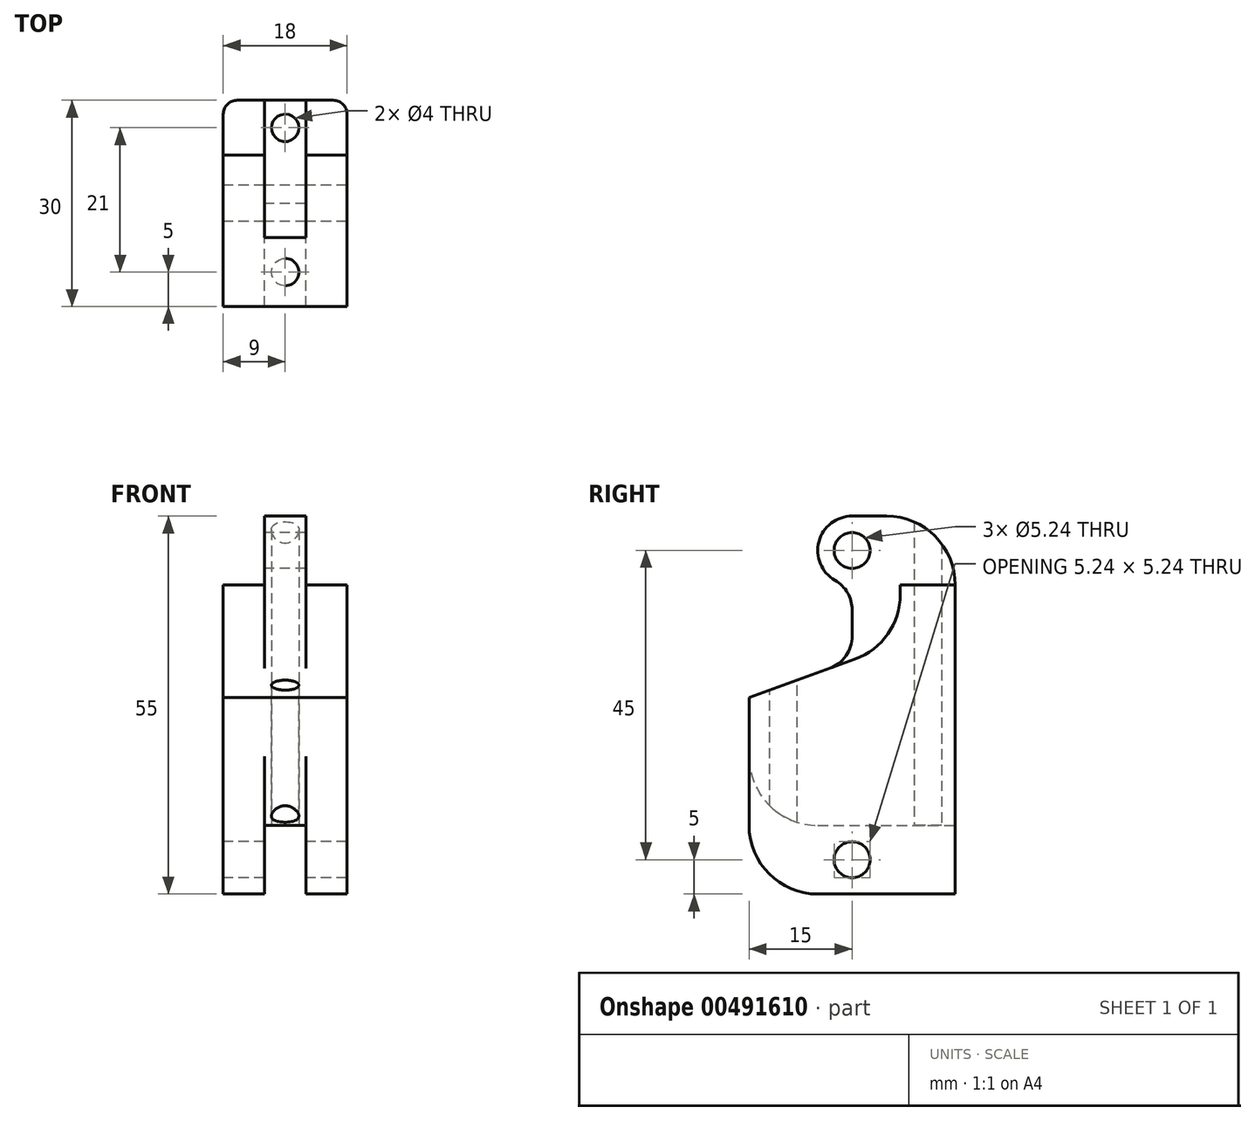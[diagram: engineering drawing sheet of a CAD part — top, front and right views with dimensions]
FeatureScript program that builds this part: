
annotation { "Feature Type Name" : "Feature", "Feature Type Description" : "" }
export const myFeature = defineFeature(function(context is Context, id is Id, definition is map)
    precondition{}
    {
        {
            var Q0;
            Q0=qCreatedBy(makeId("Front.planeOp"),FACE);
            var sketch = newSketch(context, id + "F0", { "sketchPlane" : qUnion([Q0])});
            skLineSegment(sketch, "E0.bottom", {"start": v(9, 17.5) * mm, "end": v(3, 17.5) * mm});
            skLineSegment(sketch, "E0.top", {"start": v(3, -17.5) * mm, "end": v(-3, -17.5) * mm});
            skLineSegment(sketch, "E0.left", {"start": v(9, 17.5) * mm, "end": v(9, -17.5) * mm});
            skLineSegment(sketch, "E0.right", {"start": v(-9, 17.5) * mm, "end": v(-9, -17.5) * mm});
            skPoint(sketch, "E0.middle", {"position": v(0, 0) * mm});
            skLineSegment(sketch, "E1.bottom", {"start": v(3, 27.5) * mm, "end": v(-3, 27.5) * mm});
            skLineSegment(sketch, "E1.left", {"start": v(3, 27.5) * mm, "end": v(3, 17.5) * mm});
            skLineSegment(sketch, "E1.right", {"start": v(-3, 27.5) * mm, "end": v(-3, 17.5) * mm});
            skPoint(sketch, "E1.middle", {"position": v(0, 17.5) * mm});
            skLineSegment(sketch, "E2.top", {"start": v(-9, -27.5) * mm, "end": v(-3, -27.5) * mm});
            skLineSegment(sketch, "E2.right", {"start": v(-3, -17.5) * mm, "end": v(-3, -27.5) * mm});
            skLineSegment(sketch, "E3.MirrorCS", {"start": v(3, -17.5) * mm, "end": v(3, -27.5) * mm});
            skLineSegment(sketch, "E4.MirrorCS", {"start": v(9, -27.5) * mm, "end": v(3, -27.5) * mm});
            skLineSegment(sketch, "E5.MirrorCS", {"start": v(9, -17.5) * mm, "end": v(9, -27.5) * mm});
            skLineSegment(sketch, "E6.trimOffspring", {"start": v(-3, 17.5) * mm, "end": v(-9, 17.5) * mm});
            skLineSegment(sketch, "E7", {"start": v(-9, -17.5) * mm, "end": v(-9, -27.5) * mm});
            skSolve(sketch);
        }
        {
            var Q0;
            Q0=makeQuery(id+"F0.imprint","IMPRINT",FACE,{"disambiguationData":[TD([[makeQuery(id+"F0.imprint","IMPRINT",EDGE,{"derivedFrom":sQuery(id+"F0.wireOp",EDGE,"E0.bottom")}),1.0]])]});
            extrude(context, id + "F1", {"entities" : qUnion([Q0]), "depth" : 30 * mm, "symmetric" : true});
        }
        {
            var Q0;
            Q0=makeQuery(id+"F1.opExtrude","SWEPT_FACE",FACE,{"disambiguationData":[OSD([sQuery(id+"F0.wireOp",EDGE,"E1.right")])]});
            var sketch = newSketch(context, id + "F2", { "sketchPlane" : qUnion([Q0])});
            skLineSegment(sketch, "E8", {"start": v(0, 17.5) * mm, "end": v(0, 27.5) * mm});
            skCircle(sketch, "E9", {"center": v(0, 22.5) * mm, "radius": 2.62 * mm});
            skSolve(sketch);
        }
        {
            var Q0;
            Q0=qSketchRegion(id+"F2",true);
            extrude(context, id + "F3", {"entities" : qUnion([Q0]), "operationType" : NewBodyOperationType.REMOVE, "oppositeDirection" : true, "depth" : 6 * mm});
        }
        {
            var Q0;
            Q0=makeQuery(id+"F1.opExtrude","SWEPT_FACE",FACE,{"disambiguationData":[OSD([sQuery(id+"F0.wireOp",EDGE,"E0.right"),sQuery(id+"F0.wireOp",EDGE,"E7")])]});
            var sketch = newSketch(context, id + "F4", { "sketchPlane" : qUnion([Q0])});
            skPoint(sketch, "E10.endSnap0", {"position": v(0, -27.5) * mm});
            skCircle(sketch, "E11", {"center": v(0, -22.5) * mm, "radius": 2.62 * mm});
            skLineSegment(sketch, "E12", {"start": v(0, -27.5) * mm, "end": v(0, -22.5) * mm});
            skSolve(sketch);
        }
        {
            var Q0;
            Q0=qSketchRegion(id+"F4",true);
            extrude(context, id + "F5", {"entities" : qUnion([Q0]), "operationType" : NewBodyOperationType.REMOVE, "oppositeDirection" : true, "depth" : 18 * mm});
        }
        {
            var Q0;
            Q0=makeQuery(id+"F1.opExtrude","CAP_EDGE",EDGE,{"disambiguationData":[OSD([sQuery(id+"F0.wireOp",EDGE,"E1.bottom")])],"isStart":true});
            var Q1;
            Q1=makeQuery(id+"F1.opExtrude","CAP_EDGE",EDGE,{"disambiguationData":[OSD([sQuery(id+"F0.wireOp",EDGE,"E1.bottom")])],"isStart":false});
            var Q2;
            Q2=makeQuery(id+"F1.opExtrude","CAP_EDGE",EDGE,{"disambiguationData":[OSD([sQuery(id+"F0.wireOp",EDGE,"E4.MirrorCS")])],"isStart":false});
            var Q3;
            Q3=makeQuery(id+"F1.opExtrude","CAP_EDGE",EDGE,{"disambiguationData":[OSD([sQuery(id+"F0.wireOp",EDGE,"E2.top")])],"isStart":false});
            fillet(context, id + "F6", {"entities" : qUnion([Q0, Q1, Q2, Q3]), "radius" : 10 * mm, "tangentPropagation" : true, "allowEdgeOverflow" : false});
        }
        {
            var Q0;
            Q0=makeQuery(id+"F1.opExtrude","SWEPT_FACE",FACE,{"disambiguationData":[OSD([sQuery(id+"F0.wireOp",EDGE,"E0.left"),sQuery(id+"F0.wireOp",EDGE,"E5.MirrorCS")])]});
            var sketch = newSketch(context, id + "F7", { "sketchPlane" : qUnion([Q0])});
            skPoint(sketch, "E13.endSnap0", {"position": v(0, 17.5) * mm});
            skLineSegment(sketch, "E14", {"start": v(-15, 17.5) * mm, "end": v(-15, 1.08) * mm});
            skLineSegment(sketch, "E15", {"start": v(-15, 17.5) * mm, "end": v(7, 17.5) * mm});
            skLineSegment(sketch, "E16", {"start": v(-15, 1.08) * mm, "end": v(15, 1.08) * mm});
            skLineSegment(sketch, "E17", {"start": v(-15, 1.08) * mm, "end": v(0.42, 6.7) * mm});
            skLineSegment(sketch, "E18", {"start": v(7, 17.5) * mm, "end": v(7, 16.09) * mm});
            skPoint(sketch, "E19.visualSharp", {"position": v(7, 9.09) * mm});
            skArc(sketch, "E19.filletArc", {"start": v(0.42, 6.7) * mm, "mid": v(5.2, 10.35) * mm, "end": v(7, 16.09) * mm});
            skSolve(sketch);
        }
        {
            var Q0;
            Q0=makeQuery(id+"F1.opExtrude","SWEPT_FACE",FACE,{"disambiguationData":[OSD([sQuery(id+"F0.wireOp",EDGE,"E0.right"),sQuery(id+"F0.wireOp",EDGE,"E7")])]});
            var sketch = newSketch(context, id + "F8", { "sketchPlane" : qUnion([Q0])});
            skLineSegment(sketch, "E20", {"start": v(-0.42, 6.7) * mm, "end": v(15, 1.08) * mm});
            skLineSegment(sketch, "E21", {"start": v(15, 1.08) * mm, "end": v(15, 17.5) * mm});
            skLineSegment(sketch, "E22", {"start": v(15, 1.08) * mm, "end": v(-15, 1.08) * mm});
            skLineSegment(sketch, "E23", {"start": v(15, 17.5) * mm, "end": v(-7, 17.5) * mm});
            skLineSegment(sketch, "E24", {"start": v(-7, 17.5) * mm, "end": v(-7, 16.09) * mm});
            skPoint(sketch, "E25.visualSharp", {"position": v(-7, 9.09) * mm});
            skArc(sketch, "E25.filletArc", {"start": v(-7, 16.09) * mm, "mid": v(-5.2, 10.35) * mm, "end": v(-0.42, 6.7) * mm});
            skSolve(sketch);
        }
        {
            var Q0;
            Q0=makeQuery(id+"F8.imprint","IMPRINT",FACE,{"disambiguationData":[TD([[makeQuery(id+"F8.imprint","IMPRINT",EDGE,{"derivedFrom":sQuery(id+"F8.wireOp",EDGE,"E20")}),1.0]])]});
            extrude(context, id + "F9", {"entities" : qUnion([Q0]), "operationType" : NewBodyOperationType.REMOVE, "oppositeDirection" : true, "depth" : 6 * mm});
        }
        {
            var Q0;
            Q0=makeQuery(id+"F7.imprint","IMPRINT",FACE,{"disambiguationData":[TD([[makeQuery(id+"F7.imprint","IMPRINT",EDGE,{"derivedFrom":sQuery(id+"F7.wireOp",EDGE,"E14")}),1.0]])]});
            extrude(context, id + "F10", {"entities" : qUnion([Q0]), "operationType" : NewBodyOperationType.REMOVE, "oppositeDirection" : true, "depth" : 6 * mm});
        }
        {
            var Q0;
            Q0=makeQuery(id+"F1.opExtrude","CAP_EDGE",EDGE,{"disambiguationData":[OSD([sQuery(id+"F0.wireOp",EDGE,"E0.left"),sQuery(id+"F0.wireOp",EDGE,"E5.MirrorCS")])],"isStart":true});
            var Q1;
            Q1=makeQuery(id+"F1.opExtrude","CAP_EDGE",EDGE,{"disambiguationData":[OSD([sQuery(id+"F0.wireOp",EDGE,"E0.right"),sQuery(id+"F0.wireOp",EDGE,"E7")])],"isStart":true});
            fillet(context, id + "F11", {"entities" : qUnion([Q0, Q1]), "radius" : 2 * mm, "tangentPropagation" : true, "allowEdgeOverflow" : false});
        }
        {
            var Q0;
            Q0=makeQuery(id+"F9.boolean.opBoolean","MERGE",FACE,{"derivedFrom":[makeQuery(id+"F1.opExtrude","SWEPT_FACE",FACE,{"disambiguationData":[OSD([sQuery(id+"F0.wireOp",EDGE,"E1.right")])]}),makeQuery(id+"F9.opExtrude","CAP_FACE",FACE,{"disambiguationData":[OSD([sQuery(id+"F8.wireOp",EDGE,"E20"),sQuery(id+"F8.wireOp",EDGE,"E21"),sQuery(id+"F8.wireOp",EDGE,"E23"),sQuery(id+"F8.wireOp",EDGE,"E24"),sQuery(id+"F8.wireOp",EDGE,"E25.filletArc")])],"isStart":false})]});
            var sketch = newSketch(context, id + "F12", { "sketchPlane" : qUnion([Q0])});
            skLineSegment(sketch, "E26", {"start": v(0, 27.5) * mm, "end": v(0, 25.12) * mm});
            skCircle(sketch, "E27", {"center": v(0, 22.5) * mm, "radius": 5 * mm});
            skLineSegment(sketch, "E28", {"start": v(0, 22.5) * mm, "end": v(5, 22.5) * mm});
            skLineSegment(sketch, "E29", {"start": v(5, 22.5) * mm, "end": v(5, 4.72) * mm});
            skSolve(sketch);
        }
        {
            var Q0;
            {var subQ1=sQuery(id+"F12.wireOp",EDGE,"E29");Q0=makeQuery(id+"F12.imprint","IMPRINT",FACE,{"disambiguationData":[TD([[makeQuery(id+"F12.imprint","IMPRINT",EDGE,{"derivedFrom":subQ1}),1.0]])]});}
            extrude(context, id + "F13", {"entities" : qUnion([Q0]), "operationType" : NewBodyOperationType.REMOVE, "oppositeDirection" : true, "depth" : 6 * mm});
        }
        {
            var Q0;
            Q0=makeQuery(id+"F1.opExtrude","SWEPT_FACE",FACE,{"disambiguationData":[OSD([sQuery(id+"F0.wireOp",EDGE,"E0.top")])]});
            var sketch = newSketch(context, id + "F14", { "sketchPlane" : qUnion([Q0])});
            skSolve(sketch);
        }
        {
            var Q0;
            Q0=makeQuery(id+"F1.opExtrude","CAP_EDGE",EDGE,{"disambiguationData":[OSD([sQuery(id+"F0.wireOp",EDGE,"E0.top")])],"isStart":false});
            fillet(context, id + "F15", {"entities" : qUnion([Q0]), "radius" : 10 * mm, "tangentPropagation" : true, "allowEdgeOverflow" : false});
        }
        {
            var Q0;
            Q0=makeQuery(id+"F13.boolean.opBoolean","COPY",EDGE,{"derivedFrom":makeQuery(id+"F13.opExtrude","SWEPT_EDGE",EDGE,{"disambiguationData":[OSD([sQuery(id+"F12.wireOp",EDGE,"E27"),sQuery(id+"F12.wireOp",EDGE,"E28"),sQuery(id+"F12.wireOp",EDGE,"E29")])]})});
            cPlane(context, id + "F16", {"entities" : qUnion([Q0]), "cplaneType" : CPlaneType.LINE_ANGLE, "offset" : 25 * mm, "angle" : 90 * degree, "width" : 150 * mm, "height" : 150 * mm});
        }
        {
            var Q0;
            Q0=qCreatedBy(id+"F16.planeOp",FACE);
            var sketch = newSketch(context, id + "F17", { "sketchPlane" : qUnion([Q0])});
            skLineSegment(sketch, "E30", {"start": v(0, -5) * mm, "end": v(0, -15) * mm});
            skCircle(sketch, "E31", {"center": v(0, -10) * mm, "radius": 2 * mm});
            skSolve(sketch);
        }
        {
            var Q0;
            {var subQ0=sQuery(id+"F17.wireOp",EDGE,"E31");var subQ1=sQuery(id+"F17.wireOp",EDGE,"E30");var subQ2=makeQuery(id+"F17.imprint","INTERSECT",VERTEX,{"disambiguationData":[OD(0.0)],"derivedFrom":[subQ1,subQ0]});Q0=makeQuery(id+"F17.imprint","IMPRINT",FACE,{"disambiguationData":[TD([[makeQuery(id+"F17.imprint","IMPRINT",EDGE,{"disambiguationData":[TD([[subQ2,1.0]])],"derivedFrom":subQ1}),-1.0]])]});}
            var Q1;
            {var subQ0=sQuery(id+"F17.wireOp",EDGE,"E31");var subQ1=sQuery(id+"F17.wireOp",EDGE,"E30");var subQ2=makeQuery(id+"F17.imprint","INTERSECT",VERTEX,{"disambiguationData":[OD(0.0)],"derivedFrom":[subQ1,subQ0]});Q1=makeQuery(id+"F17.imprint","IMPRINT",FACE,{"disambiguationData":[TD([[makeQuery(id+"F17.imprint","IMPRINT",EDGE,{"disambiguationData":[TD([[subQ2,1.0]])],"derivedFrom":subQ1}),1.0]])]});}
            extrude(context, id + "F18", {"entities" : qUnion([Q0, Q1]), "operationType" : NewBodyOperationType.REMOVE, "oppositeDirection" : true, "depth" : 40 * mm});
        }
        {
            var Q0;
            {var subQ0=sQuery(id+"F0.wireOp",EDGE,"E0.top");Q0=makeQuery(id+"F14.imprint","IMPRINT",FACE,{"disambiguationData":[TD([[makeQuery(id+"F14.imprint","IMPRINT",EDGE,{"derivedFrom":makeQuery(id+"F1.opExtrude","CAP_EDGE",EDGE,{"disambiguationData":[OSD([subQ0])],"isStart":true})}),-1.0]])]});}
            var sketch = newSketch(context, id + "F19", { "sketchPlane" : qUnion([Q0])});
            skLineSegment(sketch, "E32", {"start": v(0, -15) * mm, "end": v(0, -11) * mm});
            skCircle(sketch, "E33", {"center": v(0, -11) * mm, "radius": 2 * mm});
            skLineSegment(sketch, "E34", {"start": v(0, -11) * mm, "end": v(0, -9) * mm});
            skLineSegment(sketch, "E35", {"start": v(0, -9) * mm, "end": v(0, -6.95) * mm});
            skSolve(sketch);
        }
        {
            var Q0;
            Q0 = qSketchRegion(id + "F19", true);
            extrude(context, id + "F20", {"entities" : qUnion([Q0]), "operationType" : NewBodyOperationType.REMOVE, "oppositeDirection" : true, "depth" : 45 * mm});
        }
        {
            var Q0;
            Q0=makeQuery(id+"F9.boolean.opBoolean","MERGE",FACE,{"derivedFrom":[makeQuery(id+"F1.opExtrude","SWEPT_FACE",FACE,{"disambiguationData":[OSD([sQuery(id+"F0.wireOp",EDGE,"E1.right")])]}),makeQuery(id+"F9.opExtrude","CAP_FACE",FACE,{"disambiguationData":[OSD([sQuery(id+"F8.wireOp",EDGE,"E20"),sQuery(id+"F8.wireOp",EDGE,"E21"),sQuery(id+"F8.wireOp",EDGE,"E23"),sQuery(id+"F8.wireOp",EDGE,"E24"),sQuery(id+"F8.wireOp",EDGE,"E25.filletArc")])],"isStart":false})]});
            var sketch = newSketch(context, id + "F21", { "sketchPlane" : qUnion([Q0])});
            skArc(sketch, "E36", {"start": v(0, 17.5) * mm, "mid": v(3.54, 18.96) * mm, "end": v(5, 22.5) * mm});
            skLineSegment(sketch, "E37", {"start": v(5, 22.5) * mm, "end": v(5, 4.72) * mm});
            skLineSegment(sketch, "E38", {"start": v(0, 17.5) * mm, "end": v(0, 6.54) * mm});
            skSolve(sketch);
        }
        {
            var Q0;
            Q0=makeQuery(id+"F21.imprint","IMPRINT",FACE,{"disambiguationData":[TD([[makeQuery(id+"F21.imprint","IMPRINT",EDGE,{"derivedFrom":sQuery(id+"F21.wireOp",EDGE,"E36")}),-1.0]])]});
            extrude(context, id + "F22", {"entities" : qUnion([Q0]), "operationType" : NewBodyOperationType.REMOVE, "oppositeDirection" : true, "depth" : 6 * mm});
        }
        {
            var Q0;
            Q0=makeQuery(id+"F22.boolean.opBoolean","COPY",EDGE,{"derivedFrom":makeQuery(id+"F22.opExtrude","SWEPT_EDGE",EDGE,{"disambiguationData":[OSD([sQuery(id+"F21.wireOp",EDGE,"E36"),sQuery(id+"F21.wireOp",EDGE,"E38")])]})});
            var Q1;
            Q1=makeQuery(id+"F22.boolean.opBoolean","COPY",EDGE,{"derivedFrom":makeQuery(id+"F22.opExtrude","SWEPT_EDGE",EDGE,{"disambiguationData":[OSD([sQuery(id+"F8.wireOp",EDGE,"E20"),sQuery(id+"F21.wireOp",EDGE,"E38")])]})});
            fillet(context, id + "F23", {"entities" : qUnion([Q0, Q1]), "radius" : 5 * mm, "tangentPropagation" : true, "allowEdgeOverflow" : false});
        }
    });
